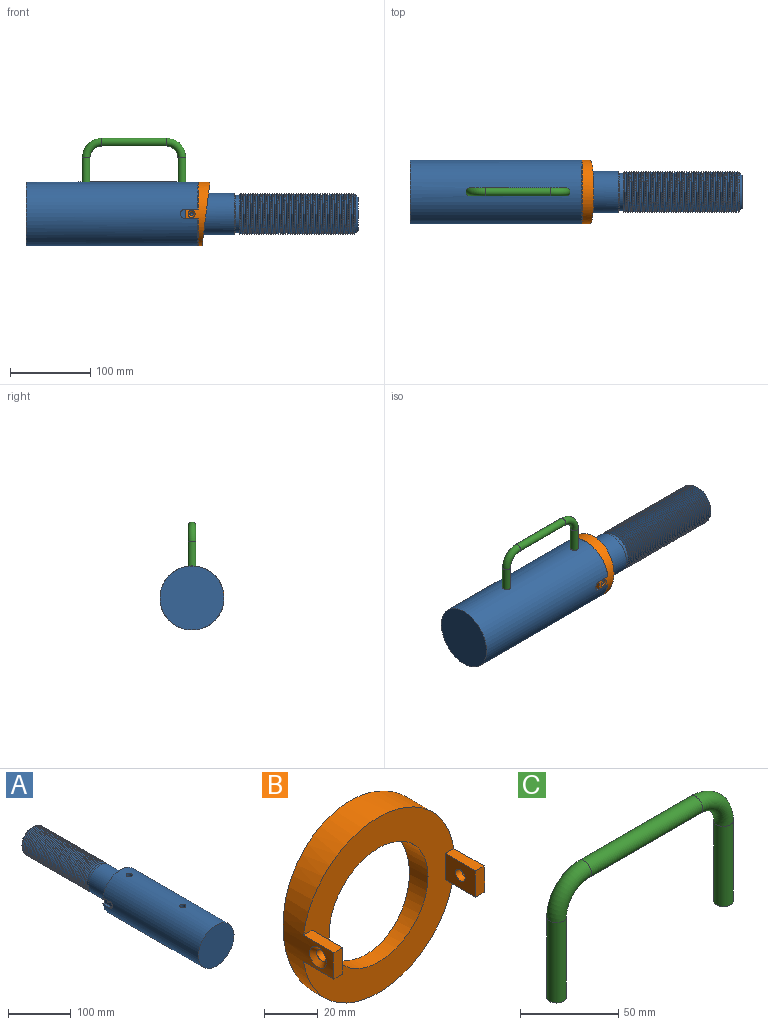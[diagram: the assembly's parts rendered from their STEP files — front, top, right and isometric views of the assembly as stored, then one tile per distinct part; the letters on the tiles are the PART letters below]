
ASSEMBLY  parts=3 mates=2
PART A: 30 faces, bbox 80x415x80 mm
  f0: cylinder r=26mm len=0mm, axis (0,-1,0), area 0mm2, adj f23,f25
  f1: cylinder r=26mm len=52mm, axis (0,-1,0), area 7351.3mm2, adj f22,f29
  f2: cylinder r=40mm len=215mm, axis (0,1,0), area 53379.7mm2, adj f3,f4,f5,f7,f9,f10,f11,f13
  f3: plane 80x79.1mm, normal (0,1,0), area 2619.9mm2, adj f2,f10,f11,f12,f14,f15,f16,f29
  f4: plane 80x80mm, normal (0,-1,0), area 5026.5mm2, adj f2
  f5: cylinder r=5mm len=20mm, axis (0,0,1), area 623.4mm2, adj f2,f6
  f6: cone r=0mm half-angle=59deg, axis (0,0,1), area 91.6mm2, adj f5
  f7: cylinder r=5mm len=20mm, axis (0,0,1), area 623.4mm2, adj f2,f8
  f8: cone r=0mm half-angle=59deg, axis (0,0,1), area 91.6mm2, adj f7
  f9: cylinder r=6mm len=12mm, axis (1,0,0), area 85.7mm2, adj f2,f10,f11,f12
  f10: plane 16x4.55mm, normal (0,0,-1), area 72.8mm2, adj f2,f3,f9,f12
  f11: plane 16x4.55mm, normal (0,0,1), area 72.8mm2, adj f2,f3,f9,f12
  f12: plane 22x12mm, normal (1,0,0), area 234.7mm2, adj f3,f9,f10,f11,f18
  f13: cylinder r=6mm len=12mm, axis (-1,0,0), area 85.7mm2, adj f2,f14,f15,f16
  f14: plane 16x4.55mm, normal (0,0,-1), area 72.8mm2, adj f2,f3,f13,f16
  f15: plane 16x4.55mm, normal (0,0,1), area 72.8mm2, adj f2,f3,f13,f16
  f16: plane 22x12mm, normal (-1,0,0), area 234.7mm2, adj f3,f13,f14,f15,f20
  f17: cone r=0mm half-angle=59deg, axis (1,0,0), area 16.2mm2, adj f18
  f18: cylinder r=2.1mm len=12.4mm, axis (1,0,0), area 163.6mm2, adj f12,f17
  f19: cone r=0mm half-angle=59deg, axis (-1,0,0), area 16.2mm2, adj f20
  f20: cylinder r=2.1mm len=12.4mm, axis (-1,0,0), area 163.6mm2, adj f16,f19
  f21: cylinder r=23.4mm len=46.8mm, axis (0,1,0), area 735.2mm2, adj f23,f28
  f22: plane 52x52mm, normal (0,1,0), area 253mm2, adj f1,f28
  f23: plane 49.47x49.47mm, normal (0,-1,0), area 198.3mm2, adj f0,f21,f24,f25
  f24: bspline ~149x60.04mm, area 22465.3mm2, adj f23,f25,f26
  f25: bspline ~147.5x60.04mm, area 22212.9mm2, adj f0,f23,f24,f26
  f26: cone r=26mm half-angle=45deg, axis (0,-1,0), area 754mm2, adj f24,f25,f27
  f27: plane 42x42mm, normal (0,1,0), area 1385.4mm2, adj f26
  f28: torus R=24.4mm, axis (0,1,0), area 234.6mm2, adj f21,f22
  f29: torus R=27mm, axis (0,-1,0), area 260.2mm2, adj f1,f3
PART B: 17 faces, bbox 80x31x80 mm
  f0: cylinder r=26mm len=52mm, axis (0,1,0), area 1635.6mm2, adj f5,f16
  f1: plane 12x5mm, normal (0,-1,0), area 58.2mm2, adj f2,f7,f8,f11
  f2: cylinder r=40mm len=80mm, axis (0,1,0), area 2775.9mm2, adj f1,f3,f4,f5,f6,f7,f8,f9
  f3: plane 12x5mm, normal (0,-1,0), area 58.2mm2, adj f2,f6,f9,f10
  f4: plane 7.11x0.16mm, normal (0,1,0), area 0.7mm2, adj f2,f16
  f5: plane 80x79.1mm, normal (0,-1,0), area 2786.4mm2, adj f0,f2,f6,f7,f8,f9,f10,f11
  f6: plane 16x4.55mm, normal (0,0,1), area 72.8mm2, adj f2,f3,f5,f10
  f7: plane 16x4.55mm, normal (0,0,1), area 72.8mm2, adj f1,f2,f5,f11
  f8: plane 16x4.55mm, normal (0,0,-1), area 72.8mm2, adj f1,f2,f5,f11
  f9: plane 16x4.55mm, normal (0,0,-1), area 72.8mm2, adj f2,f3,f5,f10
  f10: plane 16x12mm, normal (-1,0,0), area 172.4mm2, adj f3,f5,f6,f9,f13
  f11: plane 16x12mm, normal (1,0,0), area 172.4mm2, adj f1,f5,f7,f8,f12
  f12: cylinder r=2.5mm len=5mm, axis (1,0,0), area 45.1mm2, adj f11,f15
  f13: cylinder r=2.5mm len=5mm, axis (1,0,0), area 45.1mm2, adj f10,f14
  f14: bspline ~9.18x8.75mm, area 60mm2, adj f2,f13
  f15: bspline ~9.18x8.75mm, area 60mm2, adj f2,f12
  f16: plane 80x79.84mm, normal (0,0.99,-0.12), area 2924.7mm2, adj f0,f2,f4
PART C: 7 faces, bbox 134.1x10x77.1 mm
  f0: plane 10x10mm, normal (0,0,-1), area 78.5mm2, adj f2
  f1: plane 10x10mm, normal (0,0,-1), area 78.5mm2, adj f6
  f2: cylinder r=5mm len=50mm, axis (0,0,1), area 1570.8mm2, adj f0,f3
  f3: torus R=20mm, axis (0,1,0), area 987mm2, adj f2,f4
  f4: cylinder r=5mm len=80mm, axis (1,0,0), area 2513.3mm2, adj f3,f5
  f5: torus R=20mm, axis (0,1,0), area 987mm2, adj f4,f6
  f6: cylinder r=5mm len=50mm, axis (0,0,-1), area 1570.8mm2, adj f1,f5
PLACE A rot(axis=(0,0,-1),90deg) t=(82.23,-160.52,11.49)mm
PLACE B rot(axis=(0,0,-1),90deg) t=(97.23,-160.52,11.49)mm
PLACE C t=(2.23,-160.52,31.49)mm
MATE cylindrical B.f12 <-> A.f17  axis (0,1,0) through (74.23,-195.52,11.49)mm
MATE cylindrical A.f7 <-> C.f6  axis (0,0,1) through (62.23,-160.52,31.49)mm
